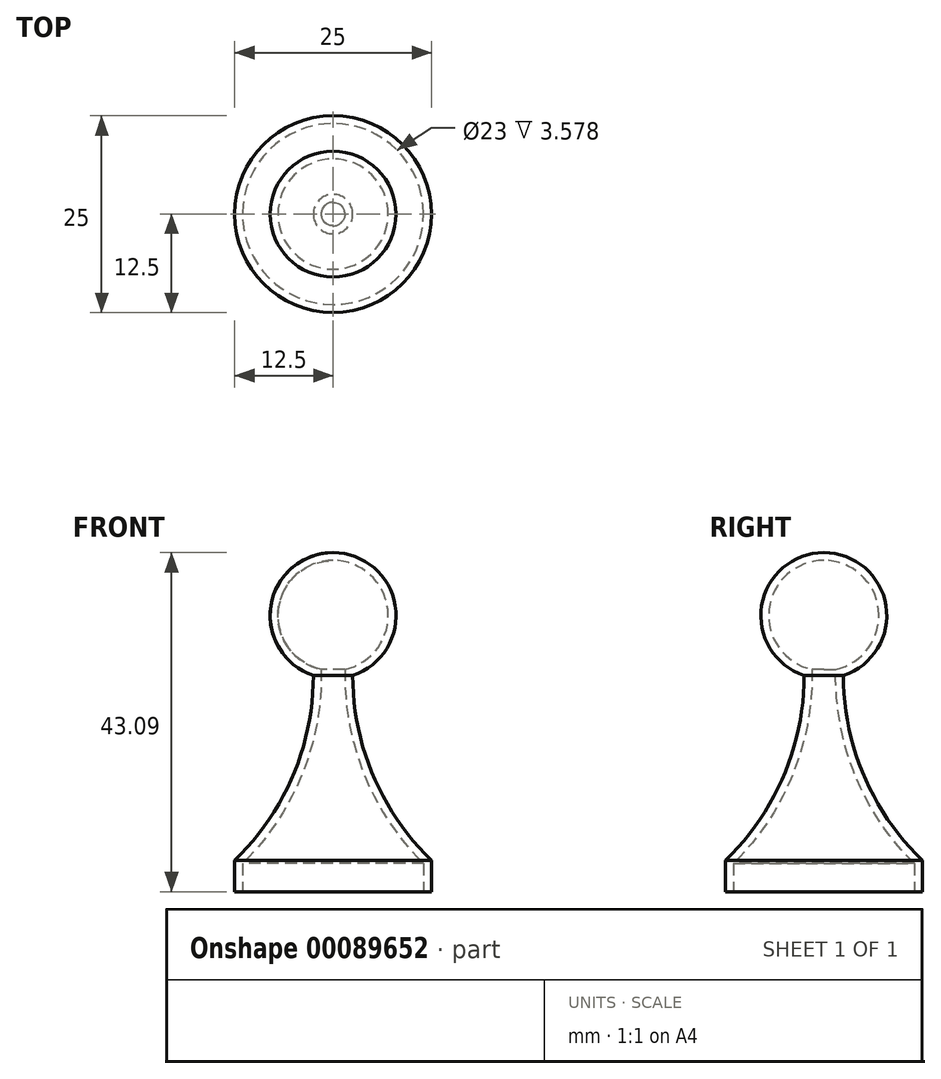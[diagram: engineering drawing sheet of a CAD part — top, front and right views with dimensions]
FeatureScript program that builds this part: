
annotation { "Feature Type Name" : "Feature", "Feature Type Description" : "" }
export const myFeature = defineFeature(function(context is Context, id is Id, definition is map)
    precondition{}
    {
        {
            var Q0;
            Q0=qCreatedBy(makeId("Front.planeOp"),FACE);
            var sketch = newSketch(context, id + "F0", { "sketchPlane" : qUnion([Q0])});
            skLineSegment(sketch, "E0.bottom", {"start": v(0, 0) * mm, "end": v(-12.5, 0) * mm});
            skLineSegment(sketch, "E0.top", {"start": v(0, 4) * mm, "end": v(-12.5, 4) * mm});
            skLineSegment(sketch, "E0.left", {"start": v(0, 0) * mm, "end": v(0, 4) * mm});
            skLineSegment(sketch, "E0.right", {"start": v(-12.5, 0) * mm, "end": v(-12.5, 4) * mm});
            skArc(sketch, "E1", {"start": v(0, 43.09) * mm, "mid": v(-8, 35.09) * mm, "end": v(0, 27.09) * mm});
            skLineSegment(sketch, "E2", {"start": v(0, 27.09) * mm, "end": v(0, 4) * mm});
            skLineSegment(sketch, "E3", {"start": v(-2.5, 27.49) * mm, "end": v(-2.5, 4) * mm});
            skLineSegment(sketch, "E4", {"start": v(0, 43.09) * mm, "end": v(0, 27.09) * mm});
            skArc(sketch, "E5", {"start": v(-12.5, 4) * mm, "mid": v(-5.1, 14.72) * mm, "end": v(-2.5, 27.49) * mm});
            skLineSegment(sketch, "E6", {"start": v(-12.5, 0) * mm, "end": v(-12.5, -2.7) * mm});
            skLineSegment(sketch, "E7", {"start": v(-12.5, -2.7) * mm, "end": v(0, -2.7) * mm});
            skLineSegment(sketch, "E8", {"start": v(0, -2.7) * mm, "end": v(0, 0) * mm});
            skSolve(sketch);
        }
        {
            var Q0;
            {var subQ0=sQuery(id+"F0.wireOp",EDGE,"E4");Q0=makeQuery(id+"F0.imprint","IMPRINT",FACE,{"disambiguationData":[TD([[makeQuery(id+"F0.imprint","IMPRINT",EDGE,{"derivedFrom":subQ0}),-1.0]])]});}
            var Q1;
            Q1=sQuery(id+"F0.wireOp",EDGE,"E4");
            revolve(context, id + "F1", {"entities" : qUnion([Q0]), "axis" : qUnion([Q1]), "revolveType" : RevolveType.FULL});
        }
        {
            var Q0;
            {var subQ2=sQuery(id+"F0.wireOp",EDGE,"E3");Q0=makeQuery(id+"F0.imprint","IMPRINT",FACE,{"disambiguationData":[TD([[makeQuery(id+"F0.imprint","IMPRINT",EDGE,{"derivedFrom":subQ2}),-1.0]])]});}
            var Q1;
            {var subQ0=sQuery(id+"F0.wireOp",EDGE,"E2");Q1=makeQuery(id+"F0.imprint","IMPRINT",FACE,{"disambiguationData":[TD([[makeQuery(id+"F0.imprint","IMPRINT",EDGE,{"derivedFrom":subQ0}),-1.0]])]});}
            var Q2;
            Q2=sQuery(id+"F0.wireOp",EDGE,"E2");
            revolve(context, id + "F2", {"operationType" : NewBodyOperationType.ADD, "entities" : qUnion([Q0, Q1]), "axis" : qUnion([Q2]), "revolveType" : RevolveType.FULL});
        }
        {
            var Q0;
            Q0=makeQuery(id+"F0.imprint","IMPRINT",FACE,{"disambiguationData":[TD([[makeQuery(id+"F0.imprint","IMPRINT",EDGE,{"derivedFrom":sQuery(id+"F0.wireOp",EDGE,"E0.bottom")}),-1.0]])]});
            var Q1;
            {var subQ0=sQuery(id+"F0.wireOp",EDGE,"E2");Q1=makeQuery(id+"F0.imprint","IMPRINT",FACE,{"disambiguationData":[TD([[makeQuery(id+"F0.imprint","IMPRINT",EDGE,{"derivedFrom":subQ0}),-1.0]])]});}
            var Q2;
            Q2=sQuery(id+"F0.wireOp",EDGE,"E0.left");
            revolve(context, id + "F3", {"operationType" : NewBodyOperationType.ADD, "entities" : qUnion([Q0, Q1]), "axis" : qUnion([Q2]), "revolveType" : RevolveType.FULL});
        }
        {
            var Q0;
            Q0=makeQuery(id+"F0.imprint","IMPRINT",FACE,{"disambiguationData":[TD([[makeQuery(id+"F0.imprint","IMPRINT",EDGE,{"derivedFrom":sQuery(id+"F0.wireOp",EDGE,"E0.bottom")}),1.0]])]});
            var Q1;
            Q1=sQuery(id+"F0.wireOp",EDGE,"E2");
            revolve(context, id + "F4", {"operationType" : NewBodyOperationType.ADD, "entities" : qUnion([Q0]), "axis" : qUnion([Q1]), "revolveType" : RevolveType.FULL});
        }
        {
            var Q0;
            Q0=makeQuery(id+"F3.opRevolve","SWEPT_FACE",FACE,{"disambiguationData":[OSD([sQuery(id+"F0.wireOp",EDGE,"E0.bottom")])]});
            var Q1;
            Q1=makeQuery(id+"F1.opRevolve","SWEPT_BODY",BODY,{"disambiguationData":[OSD([sQuery(id+"F0.wireOp",EDGE,"E1"),sQuery(id+"F0.wireOp",EDGE,"E4")])]});
            shell(context, id + "F5", {"isHollow" : true, "entities" : qUnion([Q0]), "parts" : qUnion([Q1]), "thickness" : 1 * mm});
        }
        {
            var Q0;
            Q0=makeQuery(id+"F0.imprint","IMPRINT",FACE,{"disambiguationData":[TD([[makeQuery(id+"F0.imprint","IMPRINT",EDGE,{"derivedFrom":sQuery(id+"F0.wireOp",EDGE,"E0.bottom")}),1.0]])]});
            var Q1;
            Q1=sQuery(id+"F0.wireOp",EDGE,"E8");
            revolve(context, id + "F6", {"operationType" : NewBodyOperationType.REMOVE, "entities" : qUnion([Q0]), "axis" : qUnion([Q1]), "revolveType" : RevolveType.FULL, "oppositeDirection" : true});
        }
    });
